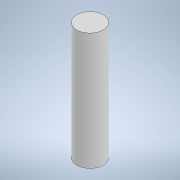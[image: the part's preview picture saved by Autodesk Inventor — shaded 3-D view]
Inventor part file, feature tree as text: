
AUTODESK INVENTOR PART (.ipt)
format: ipt  version: 2022 (Build 260153000, 153)  size: 90,112 bytes
history: native  units: mm
features: extrude x1, sketch x1
ambient origin geometry x8: Origin, YZ Plane, XZ Plane, XY Plane, X Axis, Y Axis, Z Axis, Center Point
bodies: Solide1 (feature_tree)
feature tree (2):
  extrude  "Extrusion1"  Depth=4.5mm
  sketch  "Esquisse1"
